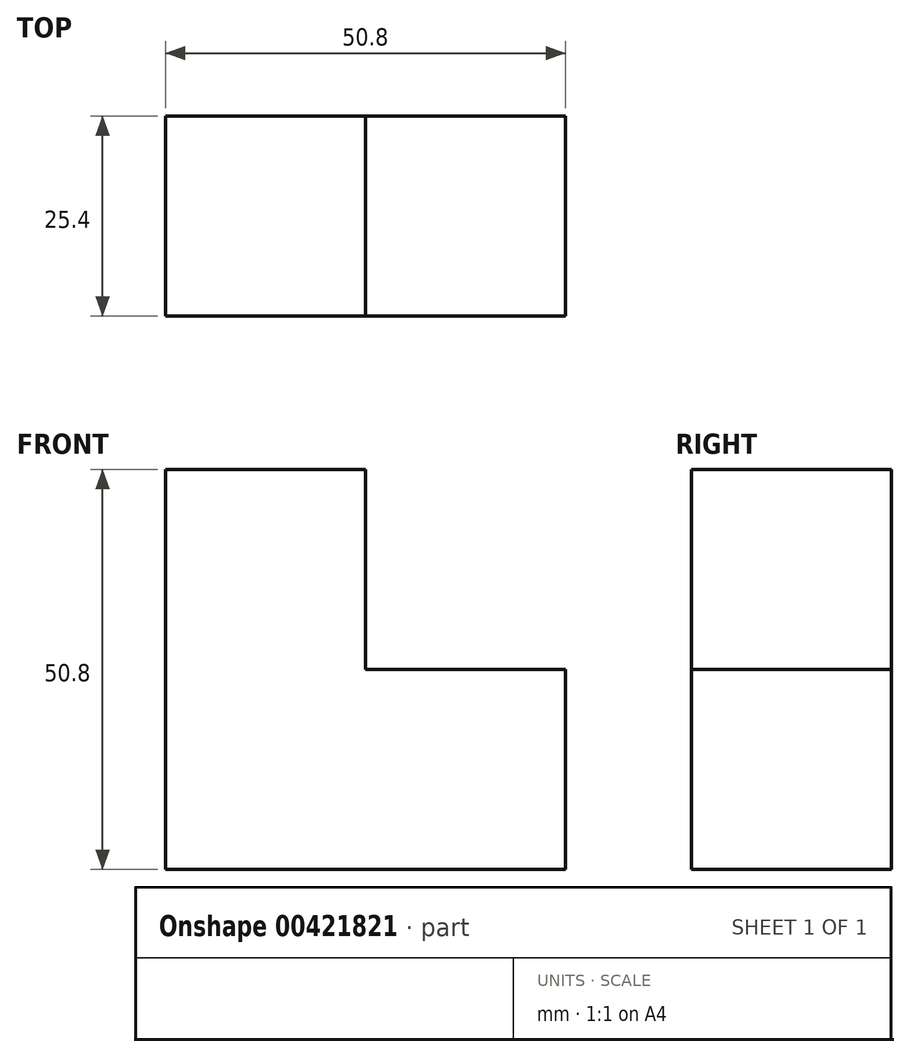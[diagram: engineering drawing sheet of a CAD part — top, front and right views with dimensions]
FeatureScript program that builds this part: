
annotation { "Feature Type Name" : "Feature", "Feature Type Description" : "" }
export const myFeature = defineFeature(function(context is Context, id is Id, definition is map)
    precondition{}
    {
        {
            var Q0;
            Q0=qCreatedBy(makeId("Front.planeOp"),FACE);
            var sketch = newSketch(context, id + "F0", { "sketchPlane" : qUnion([Q0])});
            skLineSegment(sketch, "E0", {"start": v(0, 0) * mm, "end": v(-50.8, 0) * mm});
            skLineSegment(sketch, "E1", {"start": v(-50.8, 0) * mm, "end": v(-50.8, 50.8) * mm});
            skLineSegment(sketch, "E2", {"start": v(-50.8, 50.8) * mm, "end": v(-25.4, 50.8) * mm});
            skLineSegment(sketch, "E3", {"start": v(-25.4, 50.8) * mm, "end": v(-25.4, 25.4) * mm});
            skLineSegment(sketch, "E4", {"start": v(-25.4, 25.4) * mm, "end": v(0, 25.4) * mm});
            skLineSegment(sketch, "E5", {"start": v(0, 0) * mm, "end": v(0, 25.4) * mm});
            skSolve(sketch);
        }
        {
            var Q0;
            Q0 = qSketchRegion(id + "F0", true);
            extrude(context, id + "F1", {"entities" : qUnion([Q0]), "depth" : 25.4 * mm});
        }
    });
